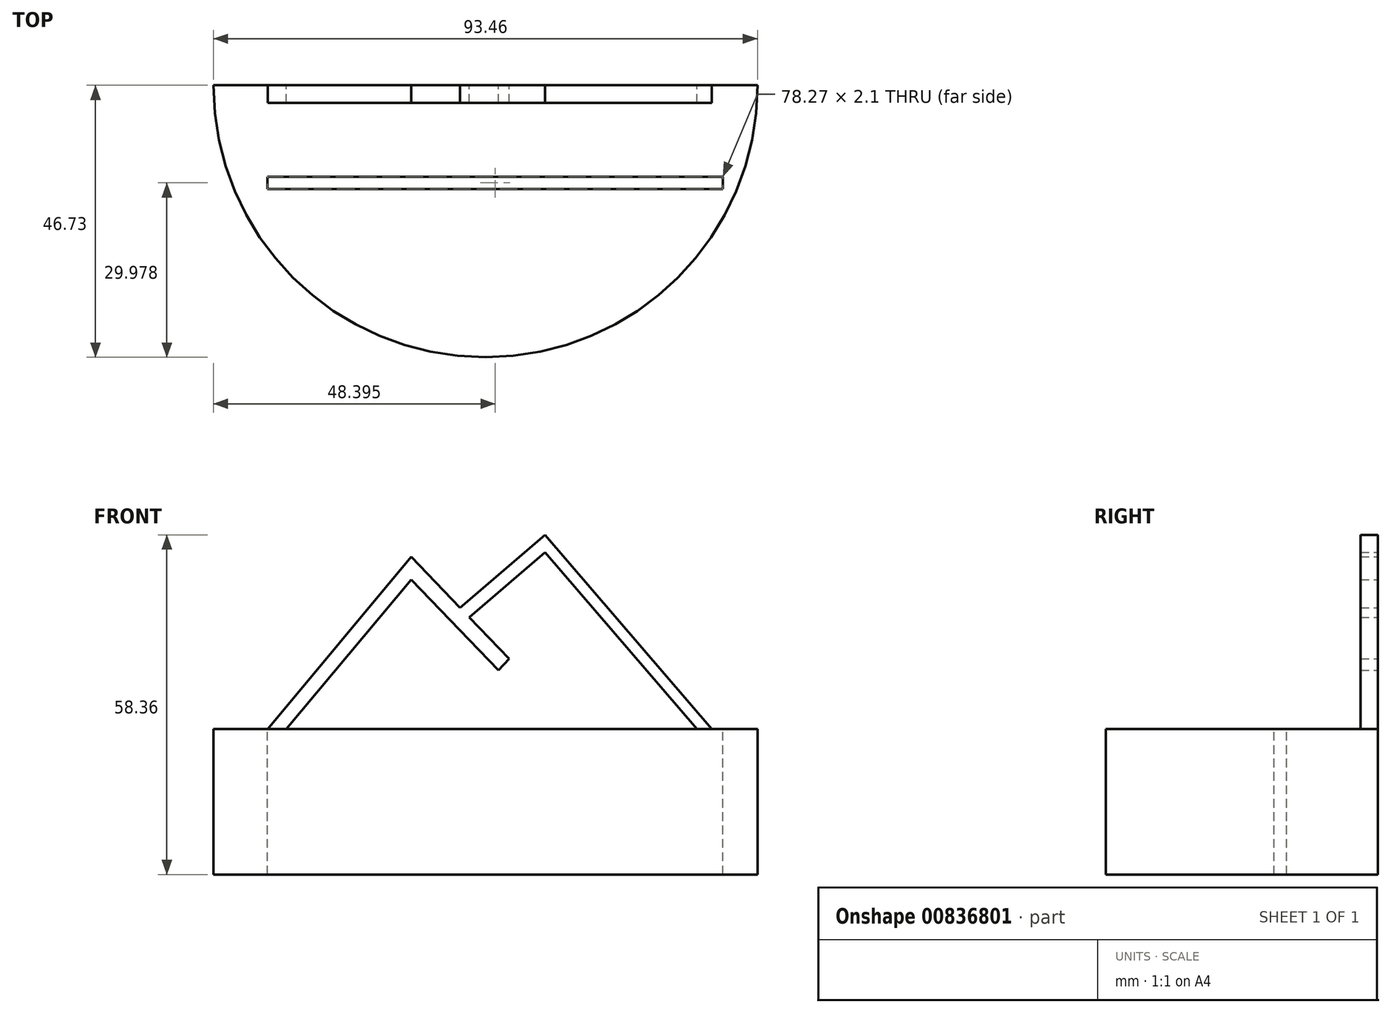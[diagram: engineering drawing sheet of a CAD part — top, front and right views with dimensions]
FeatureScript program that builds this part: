
annotation { "Feature Type Name" : "Feature", "Feature Type Description" : "" }
export const myFeature = defineFeature(function(context is Context, id is Id, definition is map)
    precondition{}
    {
        {
            var Q0;
            Q0=qCreatedBy(makeId("Top.planeOp"),FACE);
            var sketch = newSketch(context, id + "F0", { "sketchPlane" : qUnion([Q0])});
            skArc(sketch, "E0", {"start": v(-46.73, 0) * mm, "mid": v(0, -46.73) * mm, "end": v(46.73, 0) * mm});
            skLineSegment(sketch, "E1", {"start": v(-46.73, 0) * mm, "end": v(46.73, 0) * mm});
            skLineSegment(sketch, "E2.bottom", {"start": v(-37.47, -15.7) * mm, "end": v(40.8, -15.7) * mm});
            skLineSegment(sketch, "E2.top", {"start": v(-37.47, -17.8) * mm, "end": v(40.8, -17.8) * mm});
            skLineSegment(sketch, "E2.left", {"start": v(-37.47, -15.7) * mm, "end": v(-37.47, -17.8) * mm});
            skLineSegment(sketch, "E2.right", {"start": v(40.8, -15.7) * mm, "end": v(40.8, -17.8) * mm});
            skSolve(sketch);
        }
        {
            var Q0;
            Q0=qCreatedBy(makeId("Front.planeOp"),FACE);
            var sketch = newSketch(context, id + "F1", { "sketchPlane" : qUnion([Q0])});
            skLineSegment(sketch, "E3", {"start": v(-37.37, 0) * mm, "end": v(-12.78, 29.57) * mm});
            skLineSegment(sketch, "E4", {"start": v(-12.78, 29.57) * mm, "end": v(4.1, 12.07) * mm});
            skLineSegment(sketch, "E5", {"start": v(-4.34, 20.82) * mm, "end": v(10.24, 33.36) * mm});
            skLineSegment(sketch, "E6", {"start": v(10.24, 33.36) * mm, "end": v(38.9, 0) * mm});
            skLineSegment(sketch, "E7", {"start": v(38.9, 0) * mm, "end": v(-37.37, 0) * mm});
            skLineSegment(sketch, "E8", {"start": v(-34.22, 0) * mm, "end": v(-12.78, 25.68) * mm});
            skLineSegment(sketch, "E9", {"start": v(-12.78, 25.68) * mm, "end": v(2.25, 10.1) * mm});
            skLineSegment(sketch, "E10", {"start": v(2.25, 10.1) * mm, "end": v(4.1, 12.07) * mm});
            skLineSegment(sketch, "E11", {"start": v(-2.77, 19.2) * mm, "end": v(10.24, 30.37) * mm});
            skLineSegment(sketch, "E12", {"start": v(10.24, 30.37) * mm, "end": v(36.35, 0) * mm});
            skSolve(sketch);
        }
        {
            var Q0;
            Q0=makeQuery(id+"F0.imprint","IMPRINT",FACE,{"disambiguationData":[TD([[makeQuery(id+"F0.imprint","IMPRINT",EDGE,{"derivedFrom":sQuery(id+"F0.wireOp",EDGE,"E0")}),1.0]])]});
            extrude(context, id + "F2", {"entities" : qUnion([Q0]), "oppositeDirection" : true, "depth" : 25 * mm, "offsetDistance" : 25 * mm});
        }
        {
            var Q0;
            {var subQ3=sQuery(id+"F1.wireOp",EDGE,"E5");Q0=makeQuery(id+"F1.imprint","IMPRINT",FACE,{"disambiguationData":[TD([[makeQuery(id+"F1.imprint","IMPRINT",EDGE,{"derivedFrom":subQ3}),-1.0]])]});}
            var Q1;
            {var subQ4=sQuery(id+"F1.wireOp",EDGE,"E3");Q1=makeQuery(id+"F1.imprint","IMPRINT",FACE,{"disambiguationData":[TD([[makeQuery(id+"F1.imprint","IMPRINT",EDGE,{"derivedFrom":subQ4}),-1.0]])]});}
            extrude(context, id + "F3", {"entities" : qUnion([Q0, Q1]), "operationType" : NewBodyOperationType.ADD, "depth" : 3 * mm, "offsetDistance" : 25 * mm});
        }
    });
